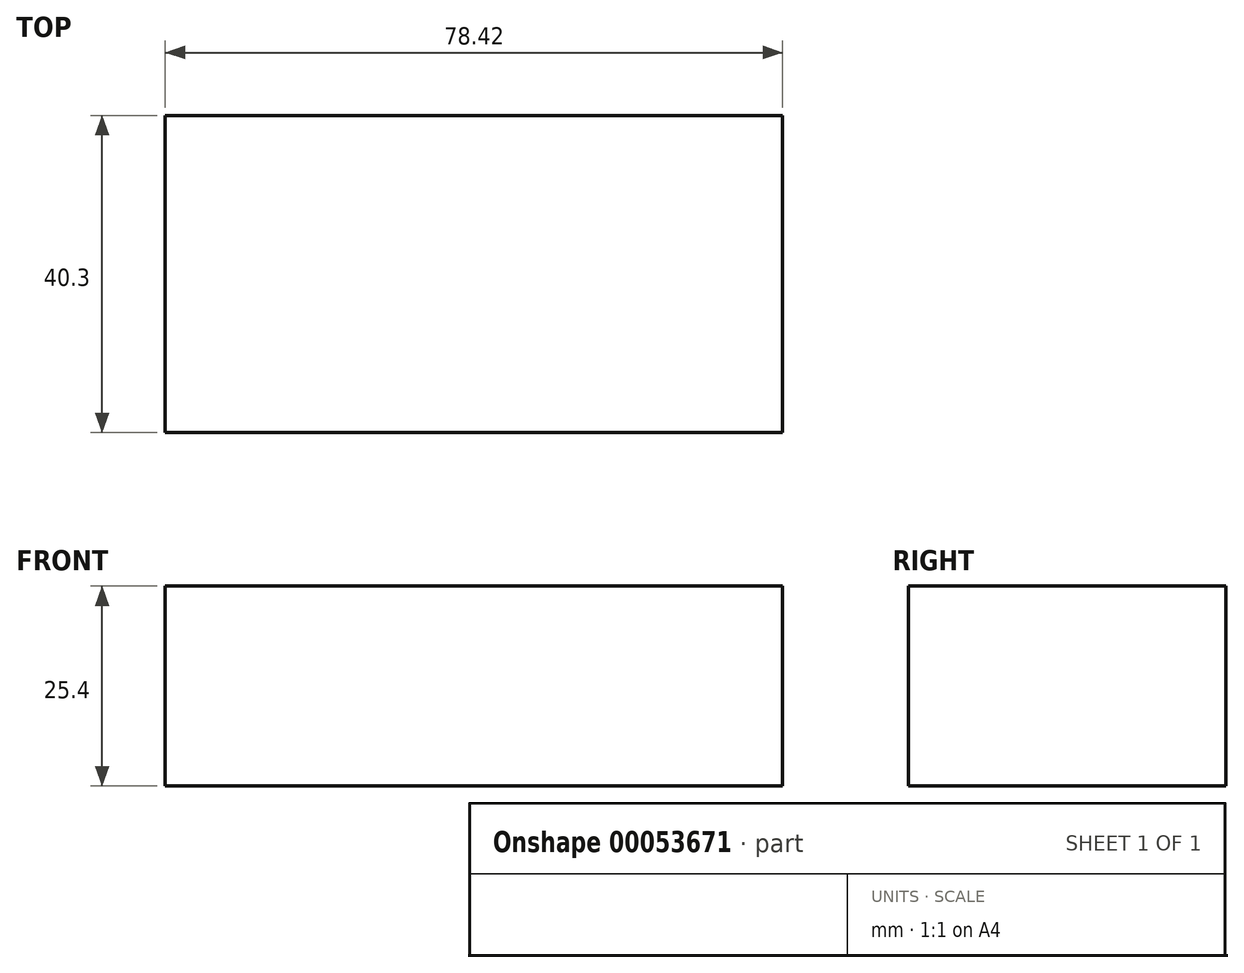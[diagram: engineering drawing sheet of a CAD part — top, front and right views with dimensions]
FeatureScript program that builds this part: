
annotation { "Feature Type Name" : "Feature", "Feature Type Description" : "" }
export const myFeature = defineFeature(function(context is Context, id is Id, definition is map)
    precondition{}
    {
        {
            var Q0;
            Q0=qCreatedBy(makeId("Top.planeOp"),FACE);
            var sketch = newSketch(context, id + "F0", { "sketchPlane" : qUnion([Q0])});
            skLineSegment(sketch, "E0.rect.bottom", {"start": v(39.21, 20.15) * mm, "end": v(-39.21, 20.15) * mm});
            skLineSegment(sketch, "E0.rect.top", {"start": v(39.21, -20.15) * mm, "end": v(-39.21, -20.15) * mm});
            skLineSegment(sketch, "E0.rect.left", {"start": v(39.21, 20.15) * mm, "end": v(39.21, -20.15) * mm});
            skLineSegment(sketch, "E0.rect.right", {"start": v(-39.21, 20.15) * mm, "end": v(-39.21, -20.15) * mm});
            skPoint(sketch, "E0.rect.middle", {"position": v(0, 0) * mm});
            skSolve(sketch);
        }
        {
            var Q0;
            Q0=makeQuery(id+"F0.imprint","IMPRINT",FACE,{"disambiguationData":[TD([[makeQuery(id+"F0.imprint","IMPRINT",EDGE,{"derivedFrom":sQuery(id+"F0.wireOp",EDGE,"E0.rect.bottom")}),1.0]])]});
            extrude(context, id + "F1", {"entities" : qUnion([Q0]), "depth" : 25.4 * mm});
        }
    });
